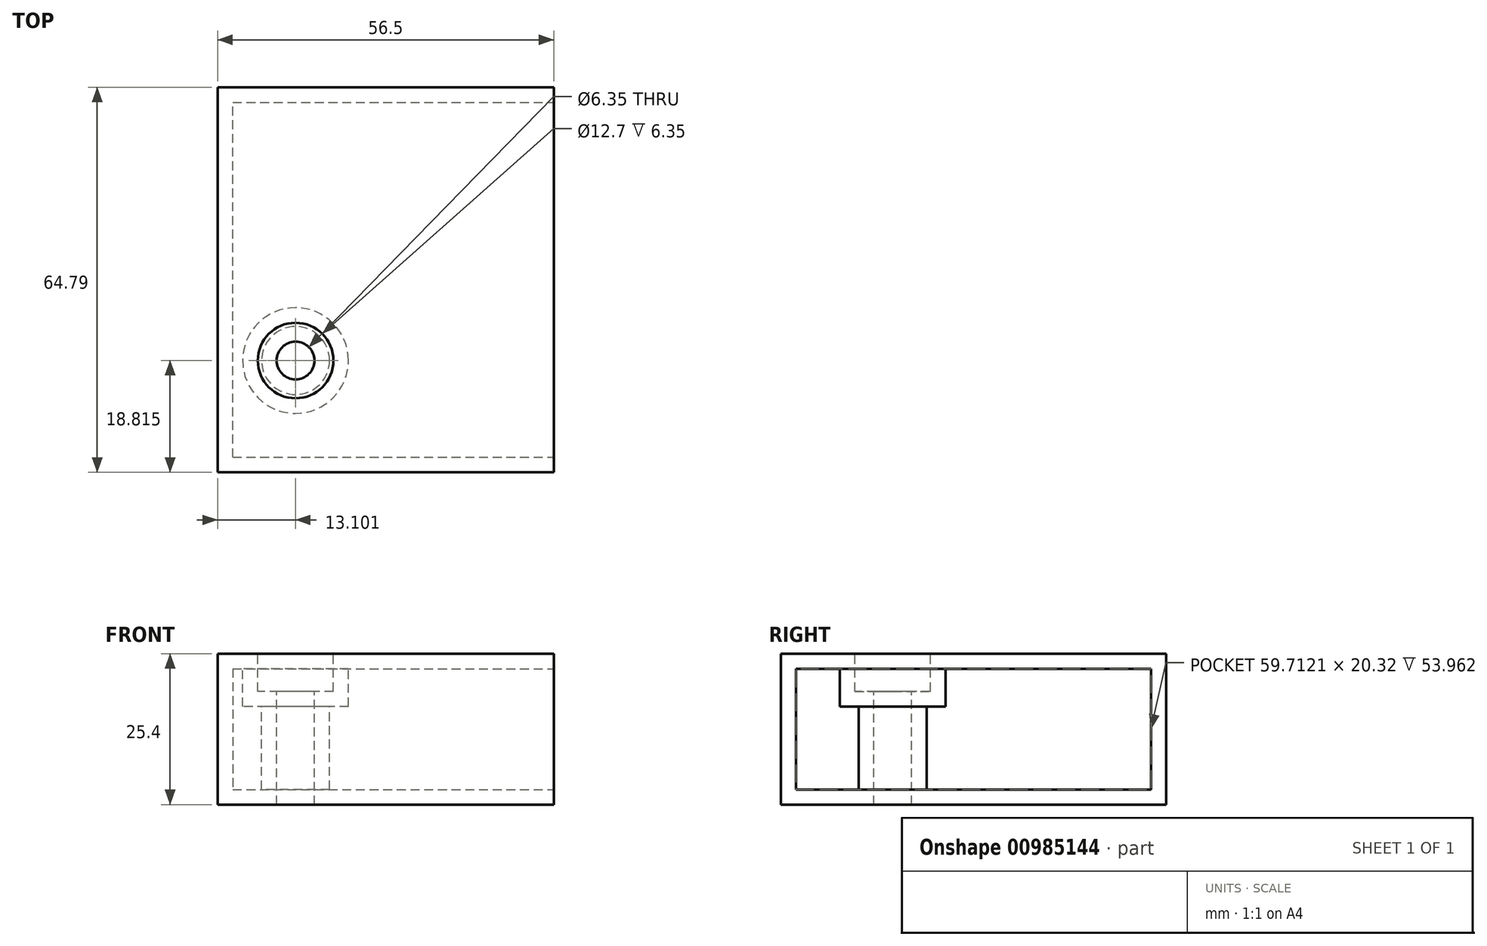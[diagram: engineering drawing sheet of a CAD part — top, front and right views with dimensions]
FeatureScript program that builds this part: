
annotation { "Feature Type Name" : "Feature", "Feature Type Description" : "" }
export const myFeature = defineFeature(function(context is Context, id is Id, definition is map)
    precondition{}
    {
        {
            var Q0;
            Q0=qCreatedBy(makeId("Top.planeOp"),FACE);
            var sketch = newSketch(context, id + "F0", { "sketchPlane" : qUnion([Q0])});
            skLineSegment(sketch, "E0.bottom", {"start": v(0, 0) * mm, "end": v(56.5, 0) * mm});
            skLineSegment(sketch, "E0.top", {"start": v(0, 64.8) * mm, "end": v(56.5, 64.8) * mm});
            skLineSegment(sketch, "E0.left", {"start": v(0, 0) * mm, "end": v(0, 64.8) * mm});
            skLineSegment(sketch, "E0.right", {"start": v(56.5, 0) * mm, "end": v(56.5, 64.8) * mm});
            skSolve(sketch);
        }
        {
            var Q0;
            Q0=makeQuery(id+"F0.imprint","IMPRINT",FACE,{"disambiguationData":[TD([[makeQuery(id+"F0.imprint","IMPRINT",EDGE,{"derivedFrom":sQuery(id+"F0.wireOp",EDGE,"E0.bottom")}),1.0]])]});
            extrude(context, id + "F1", {"entities" : qUnion([Q0]), "depth" : 25.4 * mm, "offsetDistance" : 25.4 * mm});
        }
        {
            var Q0;
            Q0=makeQuery(id+"F1.opExtrude","CAP_FACE",FACE,{"disambiguationData":[OSD([sQuery(id+"F0.wireOp",EDGE,"E0.bottom"),sQuery(id+"F0.wireOp",EDGE,"E0.top"),sQuery(id+"F0.wireOp",EDGE,"E0.left"),sQuery(id+"F0.wireOp",EDGE,"E0.right")])],"isStart":false});
            var sketch = newSketch(context, id + "F2", { "sketchPlane" : qUnion([Q0])});
            skCircle(sketch, "E1", {"center": v(13.1, 18.81) * mm, "radius": 5.58 * mm});
            skSolve(sketch);
        }
        {
            var Q0;
            Q0=sQuery(id+"F2.wireOp",VERTEX,"E1.center");
            var Q1;
            Q1=makeQuery(id+"F1.opExtrude","SWEPT_BODY",BODY,{"disambiguationData":[OSD([sQuery(id+"F0.wireOp",EDGE,"E0.bottom"),sQuery(id+"F0.wireOp",EDGE,"E0.top"),sQuery(id+"F0.wireOp",EDGE,"E0.left"),sQuery(id+"F0.wireOp",EDGE,"E0.right")])]});
            hole(context, id + "F3", {"style" : HoleStyle.C_BORE, "endStyle" : HoleEndStyle.THROUGH, "holeDiameter" : 6.35 * mm, "cBoreDiameter" : 12.7 * mm, "cBoreDepth" : 6.35 * mm, "majorDiameter" : 6.35 * mm, "isTappedThrough" : true, "tappedDepth" : 12.7 * mm, "tapClearance" : 3, "locations" : qUnion([Q0]), "scope" : qUnion([Q1])});
        }
        {
            var Q0;
            Q0=makeQuery(id+"F1.opExtrude","SWEPT_FACE",FACE,{"disambiguationData":[OSD([sQuery(id+"F0.wireOp",EDGE,"E0.right")])]});
            shell(context, id + "F4", {"entities" : qUnion([Q0]), "thickness" : 2.54 * mm});
        }
    });
